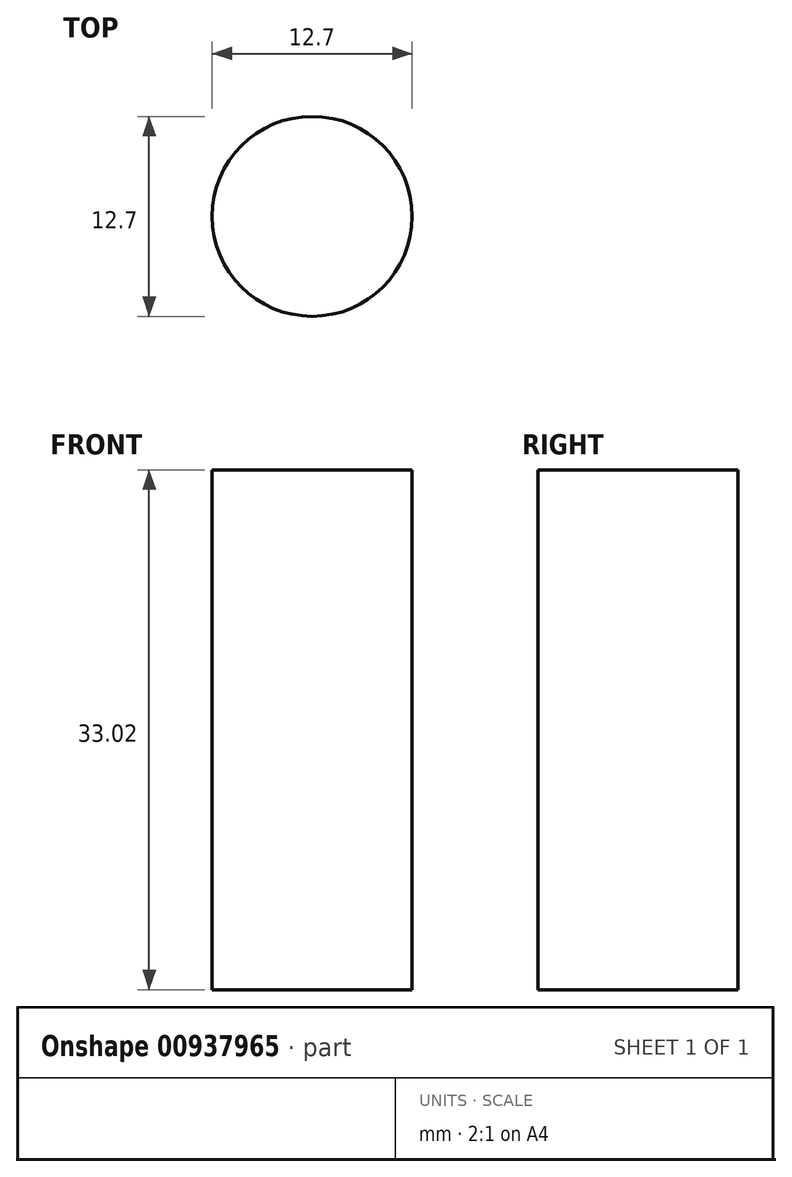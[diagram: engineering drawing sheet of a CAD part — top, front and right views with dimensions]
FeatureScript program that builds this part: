
annotation { "Feature Type Name" : "Feature", "Feature Type Description" : "" }
export const myFeature = defineFeature(function(context is Context, id is Id, definition is map)
    precondition{}
    {
        {
            var Q0;
            Q0=qCreatedBy(makeId("Top.planeOp"),FACE);
            var sketch = newSketch(context, id + "F0", { "sketchPlane" : qUnion([Q0])});
            skCircle(sketch, "E0", {"center": v(0, 0) * mm, "radius": 6.35 * mm});
            skSolve(sketch);
        }
        {
            var Q0;
            Q0 = qSketchRegion(id + "F0", true);
            extrude(context, id + "F1", {"entities" : qUnion([Q0]), "depth" : 33.02 * mm, "offsetDistance" : 25.4 * mm});
        }
    });
